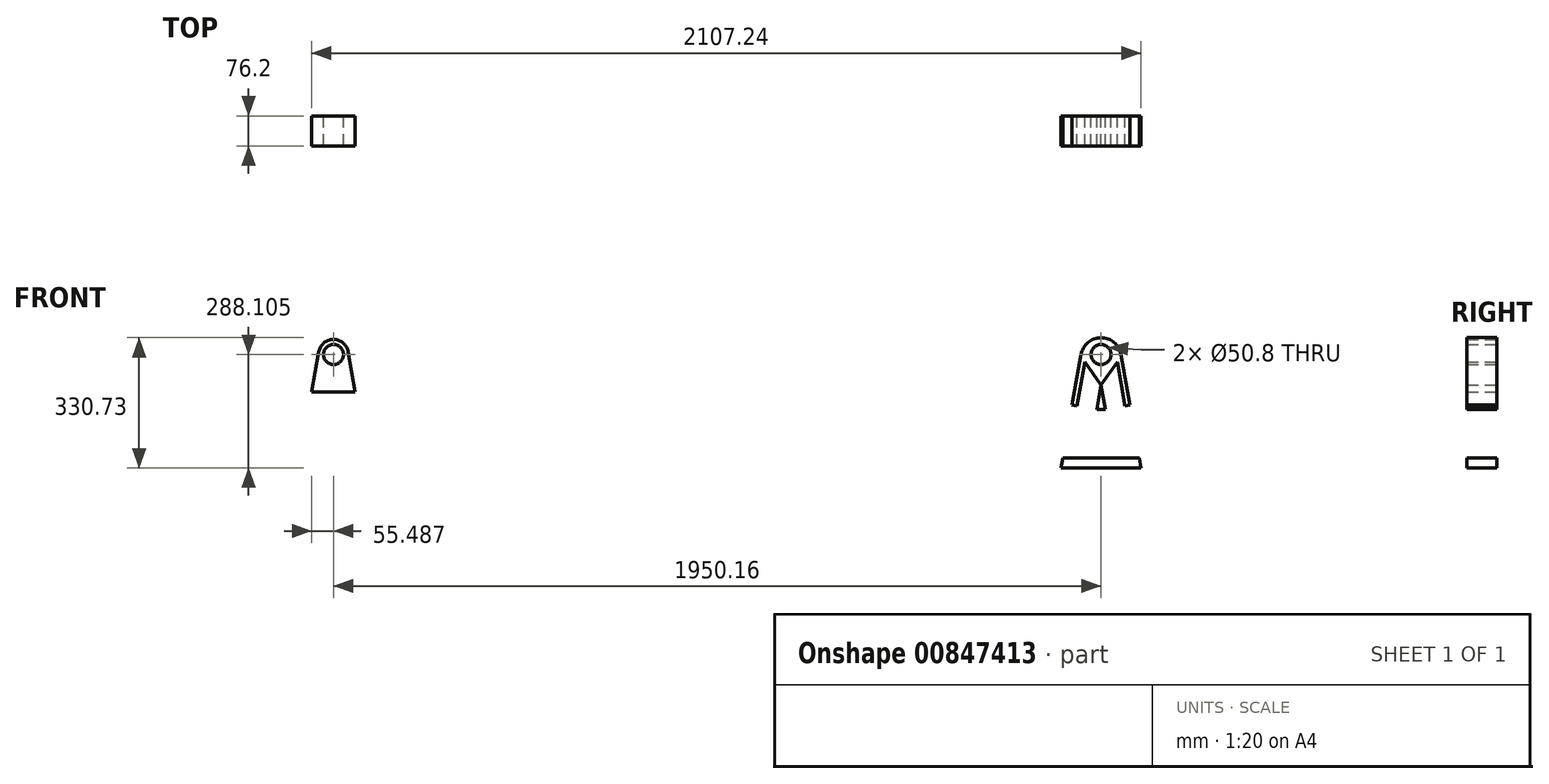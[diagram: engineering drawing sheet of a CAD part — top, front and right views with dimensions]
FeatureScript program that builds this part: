
annotation { "Feature Type Name" : "Feature", "Feature Type Description" : "" }
export const myFeature = defineFeature(function(context is Context, id is Id, definition is map)
    precondition{}
    {
        {
            var Q0;
            Q0=qCreatedBy(makeId("Front.planeOp"),FACE);
            var sketch = newSketch(context, id + "F0", { "sketchPlane" : qUnion([Q0])});
            skLineSegment(sketch, "E0", {"start": v(-24.36, 1.36) * mm, "end": v(61.37, 1.36) * mm});
            skLineSegment(sketch, "E1", {"start": v(1525.64, 0) * mm, "end": v(-556.22, 0) * mm});
            skLineSegment(sketch, "E2", {"start": v(-556.22, 0) * mm, "end": v(-556.22, 521.72) * mm});
            skLineSegment(sketch, "E3", {"start": v(-556.22, 521.72) * mm, "end": v(-1145.78, 521.72) * mm});
            skSolve(sketch);
        }
        {
            var Q0;
            Q0=qCreatedBy(makeId("Front.planeOp"),FACE);
            var sketch = newSketch(context, id + "F1", { "sketchPlane" : qUnion([Q0])});
            skLineSegment(sketch, "E4.0", {"start": v(1525.64, 0) * mm, "end": v(-556.22, 0) * mm, "construction": true});
            skLineSegment(sketch, "E4.1", {"start": v(-556.22, 0) * mm, "end": v(-556.22, 521.72) * mm, "construction": true});
            skLineSegment(sketch, "E4.2", {"start": v(-556.22, 521.72) * mm, "end": v(-1145.78, 521.72) * mm, "construction": true});
            skLineSegment(sketch, "E5", {"start": v(1329.63, 0) * mm, "end": v(1112.05, 0) * mm, "construction": true});
            skLineSegment(sketch, "E6", {"start": v(-729.31, 616.97) * mm, "end": v(1220.84, 616.97) * mm, "construction": true});
            skPoint(sketch, "E6.endSnap0", {"position": v(1220.84, 0) * mm});
            skCircle(sketch, "E7", {"center": v(-729.31, 616.97) * mm, "radius": 25.4 * mm});
            skCircle(sketch, "E8", {"center": v(1220.84, 616.97) * mm, "radius": 25.4 * mm});
            skCircle(sketch, "E9.0", {"center": v(-729.31, 616.97) * mm, "radius": 38.1 * mm});
            skLineSegment(sketch, "E10", {"start": v(-766.83, 623.58) * mm, "end": v(-784.8, 521.72) * mm});
            skLineSegment(sketch, "E11", {"start": v(-729.31, 616.97) * mm, "end": v(-729.31, 471.54) * mm, "construction": true});
            skLineSegment(sketch, "E12.MirrorCS", {"start": v(-691.8, 623.58) * mm, "end": v(-673.83, 521.72) * mm});
            skPoint(sketch, "E13.orphan", {"position": v(-695.5, 644.66) * mm});
            skPoint(sketch, "E14.orphan", {"position": v(-763.12, 644.66) * mm});
            skLineSegment(sketch, "E15", {"start": v(-784.8, 521.72) * mm, "end": v(-673.83, 521.72) * mm});
            skLineSegment(sketch, "E16", {"start": v(1220.84, 616.97) * mm, "end": v(1220.84, 0) * mm, "construction": true});
            skCircle(sketch, "E17.0", {"center": v(1220.84, 616.97) * mm, "radius": 38.1 * mm});
            skLineSegment(sketch, "E18.0", {"start": v(1245.86, 621.38) * mm, "end": v(1354.64, 4.41) * mm, "construction": true});
            skLineSegment(sketch, "E19.0", {"start": v(1195.83, 612.55) * mm, "end": v(1304.62, -4.41) * mm, "construction": true});
            skLineSegment(sketch, "E20", {"start": v(1220.84, 616.97) * mm, "end": v(1271.64, 616.97) * mm});
            skLineSegment(sketch, "E21", {"start": v(1271.64, 616.97) * mm, "end": v(1294.33, 488.3) * mm});
            skLineSegment(sketch, "E22", {"start": v(1119.24, 328.86) * mm, "end": v(1123.72, 354.26) * mm});
            skLineSegment(sketch, "E23", {"start": v(1170.04, 616.97) * mm, "end": v(1182.74, 616.97) * mm});
            skArc(sketch, "E24", {"start": v(1271.64, 616.97) * mm, "mid": v(1220.84, 659.6) * mm, "end": v(1170.04, 616.97) * mm});
            skLineSegment(sketch, "E25.0", {"start": v(1074.15, 0) * mm, "end": v(1182.55, 614.76) * mm});
            skLineSegment(sketch, "E26.0", {"start": v(1259.14, 614.76) * mm, "end": v(1367.53, 0) * mm});
            skLineSegment(sketch, "E27.trimOffspring", {"start": v(1220.84, 539.38) * mm, "end": v(1315.95, 0) * mm});
            skLineSegment(sketch, "E28.MirrorCS", {"start": v(1220.84, 539.38) * mm, "end": v(1125.73, 0) * mm});
            skPoint(sketch, "E29.orphan", {"position": v(1232.78, 471.68) * mm});
            skPoint(sketch, "E30.orphan", {"position": v(1208.9, 471.68) * mm});
            skLineSegment(sketch, "E31", {"start": v(1220.84, 539.38) * mm, "end": v(1270.87, 548.2) * mm, "construction": true});
            skLineSegment(sketch, "E32", {"start": v(1220.84, 539.38) * mm, "end": v(1170.81, 548.2) * mm, "construction": true});
            skLineSegment(sketch, "E33", {"start": v(1322.44, 328.86) * mm, "end": v(1119.24, 328.86) * mm});
            skLineSegment(sketch, "E34.0", {"start": v(1347.84, 354.26) * mm, "end": v(1119.24, 354.26) * mm});
            skLineSegment(sketch, "E35.trimOffspring", {"start": v(1147.35, 488.3) * mm, "end": v(1170.04, 616.97) * mm});
            skLineSegment(sketch, "E36.trimOffspring", {"start": v(1317.96, 354.26) * mm, "end": v(1322.44, 328.86) * mm});
            skLineSegment(sketch, "E37", {"start": v(1209.89, 477.27) * mm, "end": v(1147.35, 488.3) * mm});
            skLineSegment(sketch, "E38", {"start": v(1294.33, 488.3) * mm, "end": v(1231.8, 477.27) * mm});
            skLineSegment(sketch, "E39.trimOffspring", {"start": v(1231.8, 477.27) * mm, "end": v(1209.89, 477.27) * mm});
            skLineSegment(sketch, "E40", {"start": v(1220.84, 539.38) * mm, "end": v(1179.64, 598.23) * mm});
            skLineSegment(sketch, "E41", {"start": v(1220.84, 539.38) * mm, "end": v(1262.05, 598.23) * mm});
            skLineSegment(sketch, "E42.bottom", {"start": v(1176.53, 0) * mm, "end": v(1055.88, 0) * mm});
            skLineSegment(sketch, "E42.top", {"start": v(1176.53, 38.1) * mm, "end": v(1055.88, 38.1) * mm});
            skLineSegment(sketch, "E42.left", {"start": v(1176.53, 0) * mm, "end": v(1176.53, 38.1) * mm});
            skLineSegment(sketch, "E42.right", {"start": v(1055.88, 0) * mm, "end": v(1055.88, 38.1) * mm});
            skSolve(sketch);
        }
        {
            var Q0;
            {var subQ0=sQuery(id+"F1.wireOp",EDGE,"E10");Q0=makeQuery(id+"F1.imprint","IMPRINT",FACE,{"disambiguationData":[TD([[makeQuery(id+"F1.imprint","IMPRINT",EDGE,{"derivedFrom":subQ0}),1.0]])]});}
            var Q1;
            {var subQ0=sQuery(id+"F1.wireOp",EDGE,"E22");Q1=makeQuery(id+"F1.imprint","IMPRINT",FACE,{"disambiguationData":[TD([[makeQuery(id+"F1.imprint","IMPRINT",EDGE,{"derivedFrom":subQ0}),-1.0]])]});}
            var Q2;
            {var subQ5=sQuery(id+"F1.wireOp",EDGE,"E36.trimOffspring");Q2=makeQuery(id+"F1.imprint","IMPRINT",FACE,{"disambiguationData":[TD([[makeQuery(id+"F1.imprint","IMPRINT",EDGE,{"derivedFrom":subQ5}),-1.0]])]});}
            var Q3;
            Q3=makeQuery(id+"F1.imprint","IMPRINT",FACE,{"disambiguationData":[TD([[makeQuery(id+"F1.imprint","IMPRINT",EDGE,{"derivedFrom":sQuery(id+"F1.wireOp",EDGE,"E7")}),-1.0]])]});
            var Q4;
            {var subQ0=sQuery(id+"F1.wireOp",EDGE,"E23");Q4=makeQuery(id+"F1.imprint","IMPRINT",FACE,{"disambiguationData":[TD([[makeQuery(id+"F1.imprint","IMPRINT",EDGE,{"derivedFrom":subQ0}),1.0]])]});}
            var Q5;
            {var subQ5=sQuery(id+"F1.wireOp",EDGE,"E31");Q5=makeQuery(id+"F1.imprint","IMPRINT",FACE,{"disambiguationData":[TD([[makeQuery(id+"F1.imprint","IMPRINT",EDGE,{"derivedFrom":subQ5}),-1.0]])]});}
            var Q6;
            {var subQ5=sQuery(id+"F1.wireOp",EDGE,"E32");Q6=makeQuery(id+"F1.imprint","IMPRINT",FACE,{"disambiguationData":[TD([[makeQuery(id+"F1.imprint","IMPRINT",EDGE,{"derivedFrom":subQ5}),1.0]])]});}
            var Q7;
            {var subQ0=sQuery(id+"F1.wireOp",EDGE,"E33");var subQ1=sQuery(id+"F1.wireOp",EDGE,"E25.0");var subQ2=makeQuery(id+"F1.imprint","INTERSECT",VERTEX,{"derivedFrom":[subQ1,subQ0]});Q7=makeQuery(id+"F1.imprint","IMPRINT",FACE,{"disambiguationData":[TD([[makeQuery(id+"F1.imprint","IMPRINT",EDGE,{"disambiguationData":[TD([[subQ2,-1.0]])],"derivedFrom":subQ1}),-1.0]])]});}
            var Q8;
            {var subQ0=sQuery(id+"F1.wireOp",EDGE,"E33");var subQ1=sQuery(id+"F1.wireOp",EDGE,"E26.0");var subQ2=makeQuery(id+"F1.imprint","INTERSECT",VERTEX,{"derivedFrom":[subQ1,subQ0]});Q8=makeQuery(id+"F1.imprint","IMPRINT",FACE,{"disambiguationData":[TD([[makeQuery(id+"F1.imprint","IMPRINT",EDGE,{"disambiguationData":[TD([[subQ2,1.0]])],"derivedFrom":subQ1}),-1.0]])]});}
            var Q9;
            {var subQ0=sQuery(id+"F1.wireOp",EDGE,"E33");var subQ1=sQuery(id+"F1.wireOp",EDGE,"E27.trimOffspring");var subQ2=makeQuery(id+"F1.imprint","INTERSECT",VERTEX,{"derivedFrom":[subQ1,subQ0]});Q9=makeQuery(id+"F1.imprint","IMPRINT",FACE,{"disambiguationData":[TD([[makeQuery(id+"F1.imprint","IMPRINT",EDGE,{"disambiguationData":[TD([[subQ2,1.0]])],"derivedFrom":subQ1}),-1.0]])]});}
            var Q10;
            {var subQ9=sQuery(id+"F1.wireOp",EDGE,"E21");Q10=makeQuery(id+"F1.imprint","IMPRINT",FACE,{"disambiguationData":[TD([[makeQuery(id+"F1.imprint","IMPRINT",EDGE,{"derivedFrom":subQ9}),-1.0]])]});}
            var Q11;
            Q11=makeQuery(id+"F1.imprint","IMPRINT",FACE,{"disambiguationData":[TD([[makeQuery(id+"F1.imprint","IMPRINT",EDGE,{"derivedFrom":sQuery(id+"F1.wireOp",EDGE,"E8")}),-1.0]])]});
            var Q12;
            {var subQ3=sQuery(id+"F1.wireOp",EDGE,"E39.trimOffspring");Q12=makeQuery(id+"F1.imprint","IMPRINT",FACE,{"disambiguationData":[TD([[makeQuery(id+"F1.imprint","IMPRINT",EDGE,{"derivedFrom":subQ3}),-1.0]])]});}
            extrude(context, id + "F2", {"entities" : qUnion([Q0, Q1, Q2, Q3, Q4, Q5, Q6, Q7, Q8, Q9, Q10, Q11, Q12]), "depth" : 76.2 * mm, "offsetDistance" : 25.4 * mm});
        }
    });
